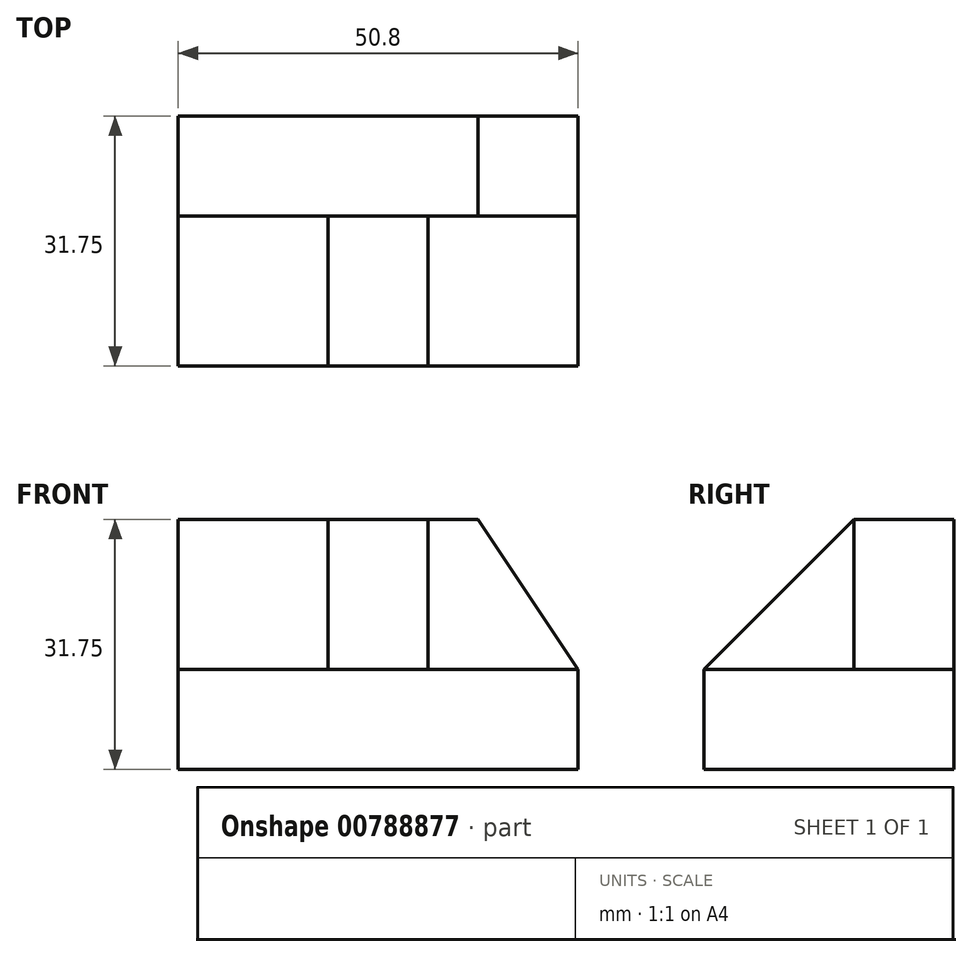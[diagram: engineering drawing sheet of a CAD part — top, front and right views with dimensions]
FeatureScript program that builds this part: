
annotation { "Feature Type Name" : "Feature", "Feature Type Description" : "" }
export const myFeature = defineFeature(function(context is Context, id is Id, definition is map)
    precondition{}
    {
        {
            var Q0;
            Q0=qCreatedBy(makeId("Top.planeOp"),FACE);
            var sketch = newSketch(context, id + "F0", { "sketchPlane" : qUnion([Q0])});
            skLineSegment(sketch, "E0", {"start": v(0, 0) * mm, "end": v(50.8, 0) * mm});
            skLineSegment(sketch, "E1", {"start": v(50.8, 0) * mm, "end": v(50.8, 31.75) * mm});
            skLineSegment(sketch, "E2", {"start": v(50.8, 31.75) * mm, "end": v(0, 31.75) * mm});
            skLineSegment(sketch, "E3", {"start": v(0, 31.75) * mm, "end": v(0, 0) * mm});
            skSolve(sketch);
        }
        {
            var Q0;
            Q0=qSketchRegion(id+"F0",true);
            extrude(context, id + "F1", {"entities" : qUnion([Q0]), "depth" : 12.7 * mm, "offsetDistance" : 25.4 * mm});
        }
        {
            var Q0;
            Q0=makeQuery(id+"F1.opExtrude","CAP_FACE",FACE,{"disambiguationData":[OSD([sQuery(id+"F0.wireOp",EDGE,"E0"),sQuery(id+"F0.wireOp",EDGE,"E1"),sQuery(id+"F0.wireOp",EDGE,"E2"),sQuery(id+"F0.wireOp",EDGE,"E3")])],"isStart":false});
            var sketch = newSketch(context, id + "F2", { "sketchPlane" : qUnion([Q0])});
            skLineSegment(sketch, "E4", {"start": v(50.8, 31.75) * mm, "end": v(50.8, 19.05) * mm});
            skLineSegment(sketch, "E5", {"start": v(50.8, 19.05) * mm, "end": v(31.75, 19.05) * mm});
            skLineSegment(sketch, "E6", {"start": v(31.75, 19.05) * mm, "end": v(31.75, 0) * mm});
            skLineSegment(sketch, "E7", {"start": v(31.75, 0) * mm, "end": v(19.05, 0) * mm});
            skLineSegment(sketch, "E8", {"start": v(19.05, 0) * mm, "end": v(19.05, 19.05) * mm});
            skLineSegment(sketch, "E9", {"start": v(19.05, 19.05) * mm, "end": v(0, 19.05) * mm});
            skSolve(sketch);
        }
        {
            var Q0;
            Q0=makeQuery(id+"F2.imprint","IMPRINT",FACE,{"disambiguationData":[TD([[makeQuery(id+"F2.imprint","IMPRINT",EDGE,{"derivedFrom":sQuery(id+"F2.wireOp",EDGE,"E4")}),1.0]])]});
            extrude(context, id + "F3", {"entities" : qUnion([Q0]), "operationType" : NewBodyOperationType.ADD, "depth" : 19.05 * mm, "offsetDistance" : 25.4 * mm});
        }
        {
            var Q0;
            Q0=makeQuery(id+"F3.opExtrude","SWEPT_FACE",FACE,{"disambiguationData":[OSD([sQuery(id+"F2.wireOp",EDGE,"E5")])]});
            var sketch = newSketch(context, id + "F4", { "sketchPlane" : qUnion([Q0])});
            skLineSegment(sketch, "E10", {"start": v(50.8, 31.75) * mm, "end": v(38.1, 31.75) * mm});
            skLineSegment(sketch, "E11", {"start": v(38.1, 31.75) * mm, "end": v(50.8, 12.7) * mm});
            skSolve(sketch);
        }
        {
            var Q0;
            Q0=makeQuery(id+"F4.imprint","IMPRINT",FACE,{"disambiguationData":[TD([[makeQuery(id+"F4.imprint","IMPRINT",EDGE,{"derivedFrom":sQuery(id+"F4.wireOp",EDGE,"E10")}),1.0]])]});
            extrude(context, id + "F5", {"entities" : qUnion([Q0]), "operationType" : NewBodyOperationType.REMOVE, "oppositeDirection" : true, "depth" : 12.7 * mm, "offsetDistance" : 25.4 * mm});
        }
        {
            var Q0;
            Q0=makeQuery(id+"F3.opExtrude","SWEPT_FACE",FACE,{"disambiguationData":[OSD([sQuery(id+"F2.wireOp",EDGE,"E6")])]});
            var sketch = newSketch(context, id + "F6", { "sketchPlane" : qUnion([Q0])});
            skLineSegment(sketch, "E12", {"start": v(19.05, 31.75) * mm, "end": v(0, 12.7) * mm});
            skSolve(sketch);
        }
        {
            var Q0;
            Q0=makeQuery(id+"F6.imprint","IMPRINT",FACE,{"disambiguationData":[TD([[makeQuery(id+"F6.imprint","IMPRINT",EDGE,{"derivedFrom":sQuery(id+"F6.wireOp",EDGE,"E12")}),-1.0]])]});
            extrude(context, id + "F7", {"entities" : qUnion([Q0]), "operationType" : NewBodyOperationType.REMOVE, "oppositeDirection" : true, "depth" : 12.7 * mm, "offsetDistance" : 25.4 * mm});
        }
    });
